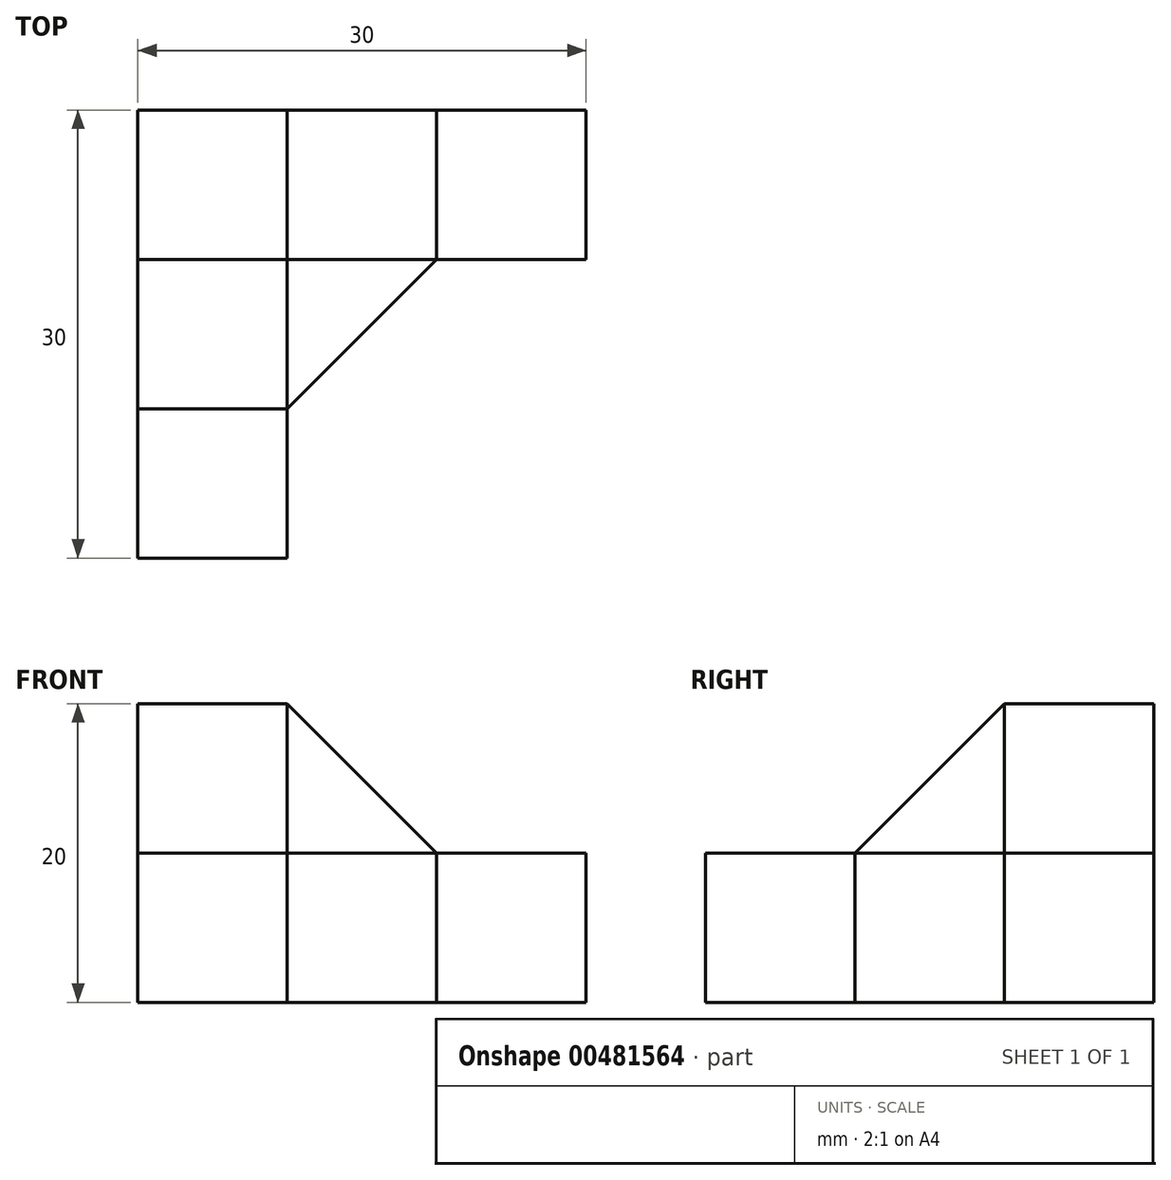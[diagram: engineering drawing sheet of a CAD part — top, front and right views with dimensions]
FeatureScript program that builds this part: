
annotation { "Feature Type Name" : "Feature", "Feature Type Description" : "" }
export const myFeature = defineFeature(function(context is Context, id is Id, definition is map)
    precondition{}
    {
        {
            var Q0;
            Q0=qCreatedBy(makeId("Front.planeOp"),FACE);
            var sketch = newSketch(context, id + "F0", { "sketchPlane" : qUnion([Q0])});
            skLineSegment(sketch, "E0.bottom", {"start": v(0, 0) * mm, "end": v(10, 0) * mm});
            skLineSegment(sketch, "E0.top", {"start": v(0, 10) * mm, "end": v(10, 10) * mm});
            skLineSegment(sketch, "E0.left", {"start": v(0, 0) * mm, "end": v(0, 10) * mm});
            skLineSegment(sketch, "E0.right", {"start": v(10, 0) * mm, "end": v(10, 10) * mm});
            skLineSegment(sketch, "E1.top", {"start": v(0, 20) * mm, "end": v(10, 20) * mm});
            skLineSegment(sketch, "E1.left", {"start": v(0, 10) * mm, "end": v(0, 20) * mm});
            skLineSegment(sketch, "E1.right", {"start": v(10, 10) * mm, "end": v(10, 20) * mm});
            skLineSegment(sketch, "E2.bottom", {"start": v(10, 0) * mm, "end": v(20, 0) * mm});
            skLineSegment(sketch, "E2.top", {"start": v(10, 10) * mm, "end": v(20, 10) * mm});
            skLineSegment(sketch, "E2.right", {"start": v(20, 0) * mm, "end": v(20, 10) * mm});
            skLineSegment(sketch, "E3.bottom", {"start": v(20, 10) * mm, "end": v(30, 10) * mm});
            skLineSegment(sketch, "E3.top", {"start": v(20, 0) * mm, "end": v(30, 0) * mm});
            skLineSegment(sketch, "E3.left", {"start": v(20, 10) * mm, "end": v(20, 0) * mm});
            skLineSegment(sketch, "E3.right", {"start": v(30, 10) * mm, "end": v(30, 0) * mm});
            skLineSegment(sketch, "E4.bottom", {"start": v(10, 20) * mm, "end": v(0, 20) * mm});
            skLineSegment(sketch, "E4.top", {"start": v(10, 30) * mm, "end": v(0, 30) * mm});
            skLineSegment(sketch, "E4.left", {"start": v(10, 20) * mm, "end": v(10, 30) * mm});
            skLineSegment(sketch, "E4.right", {"start": v(0, 20) * mm, "end": v(0, 30) * mm});
            skLineSegment(sketch, "E5", {"start": v(10, 20) * mm, "end": v(20, 10) * mm});
            skSolve(sketch);
        }
        {
            var Q0;
            Q0=makeQuery(id+"F0.imprint","IMPRINT",FACE,{"disambiguationData":[TD([[makeQuery(id+"F0.imprint","IMPRINT",EDGE,{"derivedFrom":sQuery(id+"F0.wireOp",EDGE,"E0.bottom")}),1.0]])]});
            extrude(context, id + "F1", {"entities" : qUnion([Q0]), "depth" : 30 * mm});
        }
        {
            var Q0;
            Q0=makeQuery(id+"F0.imprint","IMPRINT",FACE,{"disambiguationData":[TD([[makeQuery(id+"F0.imprint","IMPRINT",EDGE,{"derivedFrom":sQuery(id+"F0.wireOp",EDGE,"E0.top")}),1.0]])]});
            var Q1;
            Q1=makeQuery(id+"F0.imprint","IMPRINT",FACE,{"disambiguationData":[TD([[makeQuery(id+"F0.imprint","IMPRINT",EDGE,{"derivedFrom":sQuery(id+"F0.wireOp",EDGE,"E4.bottom")}),-1.0]])]});
            var Q2;
            Q2=makeQuery(id+"F0.imprint","IMPRINT",FACE,{"disambiguationData":[TD([[makeQuery(id+"F0.imprint","IMPRINT",EDGE,{"derivedFrom":sQuery(id+"F0.wireOp",EDGE,"E2.bottom")}),1.0]])]});
            var Q3;
            Q3=makeQuery(id+"F0.imprint","IMPRINT",FACE,{"disambiguationData":[TD([[makeQuery(id+"F0.imprint","IMPRINT",EDGE,{"derivedFrom":sQuery(id+"F0.wireOp",EDGE,"E3.bottom")}),-1.0]])]});
            var Q4;
            Q4=makeQuery(id+"F0.imprint","IMPRINT",FACE,{"disambiguationData":[TD([[makeQuery(id+"F0.imprint","IMPRINT",EDGE,{"derivedFrom":sQuery(id+"F0.wireOp",EDGE,"E1.right")}),-1.0]])]});
            extrude(context, id + "F2", {"entities" : qUnion([Q0, Q1, Q2, Q3, Q4]), "operationType" : NewBodyOperationType.ADD, "depth" : 10 * mm});
        }
        {
            var Q0;
            Q0=qCreatedBy(makeId("Right.planeOp"),FACE);
            var sketch = newSketch(context, id + "F3", { "sketchPlane" : qUnion([Q0])});
            skLineSegment(sketch, "E6", {"start": v(-10, 20) * mm, "end": v(-20, 10) * mm});
            skLineSegment(sketch, "E7", {"start": v(-20, 10) * mm, "end": v(-10, 10) * mm});
            skLineSegment(sketch, "E8", {"start": v(-10, 10) * mm, "end": v(-10, 20) * mm});
            skSolve(sketch);
        }
        {
            var Q0;
            Q0=makeQuery(id+"F3.imprint","IMPRINT",FACE,{"disambiguationData":[TD([[makeQuery(id+"F3.imprint","IMPRINT",EDGE,{"derivedFrom":sQuery(id+"F3.wireOp",EDGE,"E6")}),1.0]])]});
            extrude(context, id + "F4", {"entities" : qUnion([Q0]), "operationType" : NewBodyOperationType.ADD, "depth" : 10 * mm});
        }
        {
            var Q0;
            Q0=qCreatedBy(makeId("Top.planeOp"),FACE);
            var sketch = newSketch(context, id + "F5", { "sketchPlane" : qUnion([Q0])});
            skLineSegment(sketch, "E9", {"start": v(10, -20) * mm, "end": v(20, -10) * mm});
            skLineSegment(sketch, "E10", {"start": v(10, -20) * mm, "end": v(10, -10) * mm});
            skLineSegment(sketch, "E11", {"start": v(10, -10) * mm, "end": v(20, -10) * mm});
            skSolve(sketch);
        }
        {
            var Q0;
            Q0=makeQuery(id+"F5.imprint","IMPRINT",FACE,{"disambiguationData":[TD([[makeQuery(id+"F5.imprint","IMPRINT",EDGE,{"derivedFrom":sQuery(id+"F5.wireOp",EDGE,"E9")}),1.0]])]});
            extrude(context, id + "F6", {"entities" : qUnion([Q0]), "operationType" : NewBodyOperationType.ADD, "depth" : 10 * mm});
        }
        {
            var Q1;
            Q1=makeQuery(id+"F6.opExtrude","CAP_FACE",FACE,{"disambiguationData":[OSD([sQuery(id+"F5.wireOp",EDGE,"E9"),sQuery(id+"F5.wireOp",EDGE,"E11"),sQuery(id+"F5.wireOp",EDGE,"E10")])],"isStart":false});
            var Q2;
            Q2=makeQuery(id+"F4.boolean.opBoolean","MERGE",VERTEX,{"derivedFrom":[makeQuery(id+"F2.opExtrude","CAP_VERTEX",VERTEX,{"disambiguationData":[OSD([sQuery(id+"F0.wireOp",EDGE,"E1.right"),sQuery(id+"F0.wireOp",EDGE,"E4.bottom"),sQuery(id+"F0.wireOp",EDGE,"E4.left"),sQuery(id+"F0.wireOp",EDGE,"E5")])],"isStart":false}),makeQuery(id+"F4.opExtrude","CAP_VERTEX",VERTEX,{"disambiguationData":[OSD([sQuery(id+"F3.wireOp",EDGE,"E6"),sQuery(id+"F3.wireOp",EDGE,"E8")])],"isStart":false})]});
            loft(context, id + "F7", {"operationType" : NewBodyOperationType.ADD, "sheetProfilesArray" : [{ "sheetProfileEntities" : qUnion([Q1]) }, { "sheetProfileEntities" : qUnion([Q2]) }]});
        }
    });
